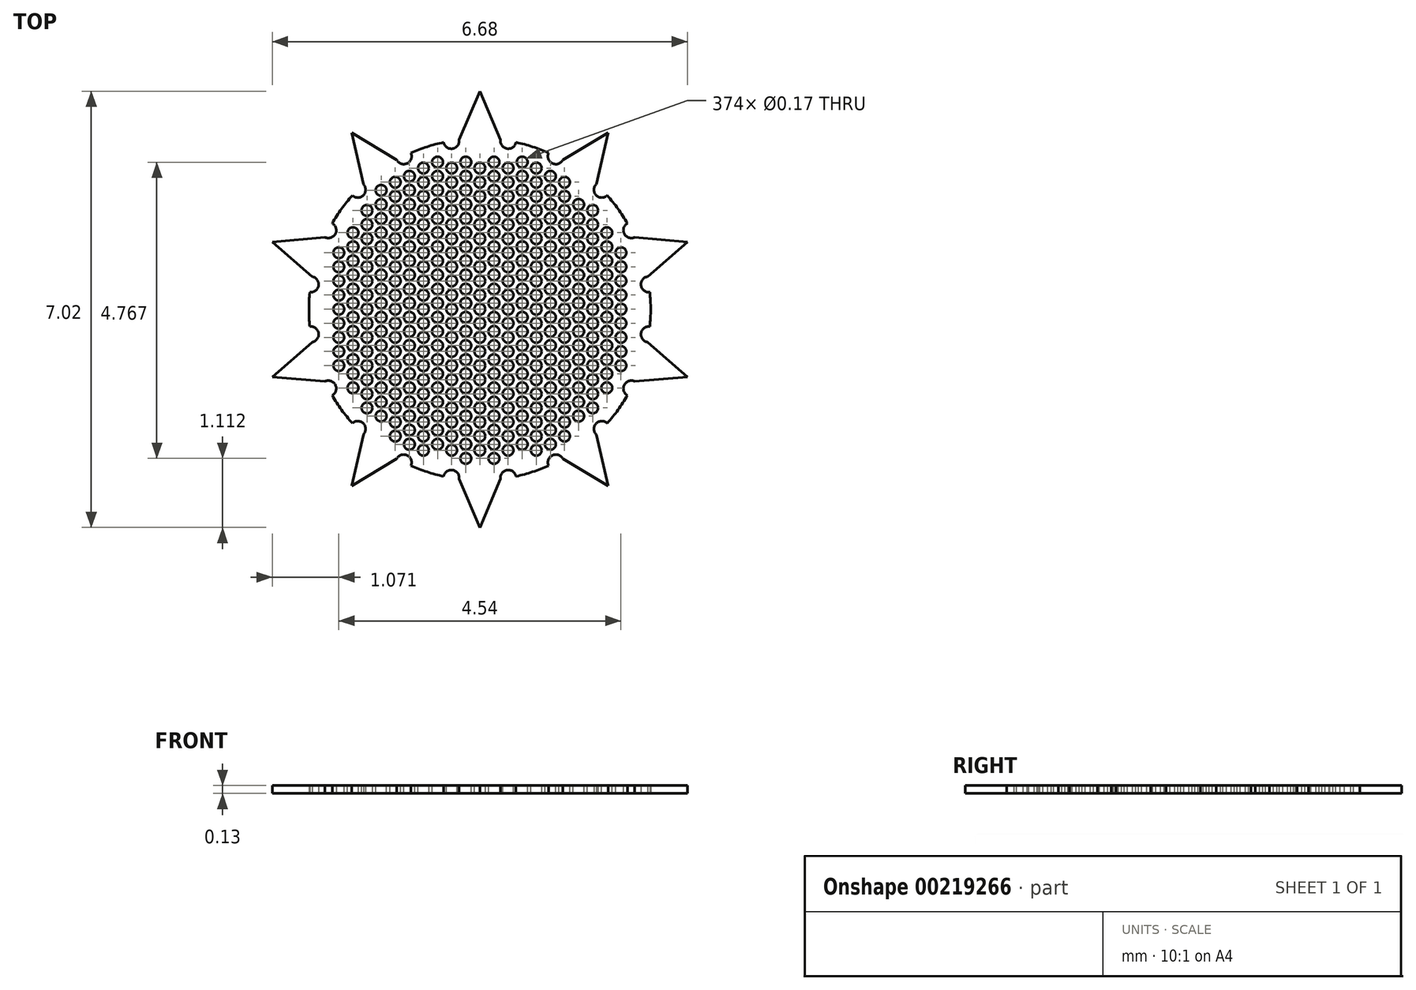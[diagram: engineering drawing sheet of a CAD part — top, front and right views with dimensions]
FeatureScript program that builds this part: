
annotation { "Feature Type Name" : "Feature", "Feature Type Description" : "" }
export const myFeature = defineFeature(function(context is Context, id is Id, definition is map)
    precondition{}
    {
        {
            var Q0;
            Q0=qCreatedBy(makeId("Top.planeOp"),FACE);
            var sketch = newSketch(context, id + "F0", { "sketchPlane" : qUnion([Q0])});
            skCircle(sketch, "E0", {"center": v(0, 0) * mm, "radius": 2.5 * mm});
            skArc(sketch, "E1", {"start": v(0.33, 2.73) * mm, "mid": v(0, 2.75) * mm, "end": v(-0.33, 2.73) * mm});
            skPoint(sketch, "E2", {"position": v(0, 2.75) * mm});
            skLineSegment(sketch, "E3", {"start": v(-3.94, 3.51) * mm, "end": v(3.7, 3.51) * mm, "construction": true});
            skLineSegment(sketch, "E4", {"start": v(0, 3.51) * mm, "end": v(-0.33, 2.73) * mm});
            skLineSegment(sketch, "E5", {"start": v(0, 3.51) * mm, "end": v(0.33, 2.73) * mm});
            skLineSegment(sketch, "E6.1.0", {"start": v(-2.06, 2.84) * mm, "end": v(-1.87, 2.01) * mm});
            skLineSegment(sketch, "E6.1.1", {"start": v(-2.06, 2.84) * mm, "end": v(-1.34, 2.4) * mm});
            skLineSegment(sketch, "E6.2.0", {"start": v(-3.34, 1.09) * mm, "end": v(-2.7, 0.53) * mm});
            skLineSegment(sketch, "E6.2.1", {"start": v(-3.34, 1.09) * mm, "end": v(-2.5, 1.16) * mm});
            skLineSegment(sketch, "E6.3.0", {"start": v(-3.34, -1.09) * mm, "end": v(-2.5, -1.16) * mm});
            skLineSegment(sketch, "E6.3.1", {"start": v(-3.34, -1.09) * mm, "end": v(-2.7, -0.53) * mm});
            skLineSegment(sketch, "E6.4.0", {"start": v(-2.06, -2.84) * mm, "end": v(-1.34, -2.4) * mm});
            skLineSegment(sketch, "E6.4.1", {"start": v(-2.06, -2.84) * mm, "end": v(-1.87, -2.01) * mm});
            skLineSegment(sketch, "E6.5.0", {"start": v(0, -3.51) * mm, "end": v(0.33, -2.73) * mm});
            skLineSegment(sketch, "E6.5.1", {"start": v(0, -3.51) * mm, "end": v(-0.33, -2.73) * mm});
            skLineSegment(sketch, "E6.6.0", {"start": v(2.06, -2.84) * mm, "end": v(1.87, -2.01) * mm});
            skLineSegment(sketch, "E6.6.1", {"start": v(2.06, -2.84) * mm, "end": v(1.34, -2.4) * mm});
            skLineSegment(sketch, "E6.7.0", {"start": v(3.34, -1.09) * mm, "end": v(2.7, -0.53) * mm});
            skLineSegment(sketch, "E6.7.1", {"start": v(3.34, -1.09) * mm, "end": v(2.5, -1.16) * mm});
            skLineSegment(sketch, "E6.8.0", {"start": v(3.34, 1.09) * mm, "end": v(2.5, 1.16) * mm});
            skLineSegment(sketch, "E6.8.1", {"start": v(3.34, 1.09) * mm, "end": v(2.7, 0.53) * mm});
            skLineSegment(sketch, "E6.9.0", {"start": v(2.06, 2.84) * mm, "end": v(1.34, 2.4) * mm});
            skLineSegment(sketch, "E6.9.1", {"start": v(2.06, 2.84) * mm, "end": v(1.87, 2.01) * mm});
            skCircle(sketch, "E7", {"center": v(0, 0) * mm, "radius": 2.62 * mm});
            skPoint(sketch, "E8", {"position": v(0.46, 2.71) * mm});
            skArc(sketch, "E9", {"start": v(0.33, 2.73) * mm, "mid": v(0.44, 2.59) * mm, "end": v(0.58, 2.69) * mm});
            skArc(sketch, "E10.1.0", {"start": v(-1.34, 2.4) * mm, "mid": v(-1.17, 2.35) * mm, "end": v(-1.1, 2.52) * mm});
            skArc(sketch, "E10.2.0", {"start": v(-2.5, 1.16) * mm, "mid": v(-2.32, 1.21) * mm, "end": v(-2.38, 1.38) * mm});
            skArc(sketch, "E10.3.0", {"start": v(-2.7, -0.53) * mm, "mid": v(-2.6, -0.38) * mm, "end": v(-2.74, -0.28) * mm});
            skArc(sketch, "E10.4.0", {"start": v(-1.87, -2.01) * mm, "mid": v(-1.87, -1.84) * mm, "end": v(-2.05, -1.83) * mm});
            skArc(sketch, "E10.5.0", {"start": v(-0.33, -2.73) * mm, "mid": v(-0.44, -2.59) * mm, "end": v(-0.58, -2.69) * mm});
            skArc(sketch, "E10.6.0", {"start": v(1.34, -2.4) * mm, "mid": v(1.17, -2.35) * mm, "end": v(1.1, -2.52) * mm});
            skArc(sketch, "E10.7.0", {"start": v(2.5, -1.16) * mm, "mid": v(2.32, -1.21) * mm, "end": v(2.38, -1.38) * mm});
            skArc(sketch, "E10.8.0", {"start": v(2.7, 0.53) * mm, "mid": v(2.6, 0.38) * mm, "end": v(2.74, 0.28) * mm});
            skArc(sketch, "E10.9.0", {"start": v(1.87, 2.01) * mm, "mid": v(1.87, 1.84) * mm, "end": v(2.05, 1.83) * mm});
            skArc(sketch, "E11", {"start": v(-0.58, 2.69) * mm, "mid": v(-0.44, 2.59) * mm, "end": v(-0.33, 2.73) * mm});
            skArc(sketch, "E12.trimOffspring", {"start": v(-0.58, 2.69) * mm, "mid": v(-0.85, 2.62) * mm, "end": v(-1.1, 2.52) * mm});
            skArc(sketch, "E13.1.0", {"start": v(-2.05, 1.83) * mm, "mid": v(-1.87, 1.84) * mm, "end": v(-1.87, 2.01) * mm});
            skArc(sketch, "E13.2.0", {"start": v(-2.74, 0.28) * mm, "mid": v(-2.6, 0.38) * mm, "end": v(-2.7, 0.53) * mm});
            skArc(sketch, "E13.3.0", {"start": v(-2.38, -1.38) * mm, "mid": v(-2.32, -1.21) * mm, "end": v(-2.5, -1.16) * mm});
            skArc(sketch, "E13.4.0", {"start": v(-1.1, -2.52) * mm, "mid": v(-1.17, -2.35) * mm, "end": v(-1.34, -2.4) * mm});
            skArc(sketch, "E13.5.0", {"start": v(0.58, -2.69) * mm, "mid": v(0.44, -2.59) * mm, "end": v(0.33, -2.73) * mm});
            skArc(sketch, "E13.6.0", {"start": v(2.05, -1.83) * mm, "mid": v(1.87, -1.84) * mm, "end": v(1.87, -2.01) * mm});
            skArc(sketch, "E13.7.0", {"start": v(2.74, -0.28) * mm, "mid": v(2.6, -0.38) * mm, "end": v(2.7, -0.53) * mm});
            skArc(sketch, "E13.8.0", {"start": v(2.38, 1.38) * mm, "mid": v(2.32, 1.21) * mm, "end": v(2.5, 1.16) * mm});
            skArc(sketch, "E13.9.0", {"start": v(1.1, 2.52) * mm, "mid": v(1.17, 2.35) * mm, "end": v(1.34, 2.4) * mm});
            skArc(sketch, "E14.trimOffspring", {"start": v(1.1, 2.52) * mm, "mid": v(0.85, 2.62) * mm, "end": v(0.58, 2.69) * mm});
            skArc(sketch, "E15.trimOffspring", {"start": v(1.87, 2.01) * mm, "mid": v(1.62, 2.22) * mm, "end": v(1.34, 2.4) * mm});
            skArc(sketch, "E16.trimOffspring", {"start": v(2.38, 1.38) * mm, "mid": v(2.22, 1.62) * mm, "end": v(2.05, 1.83) * mm});
            skArc(sketch, "E17.trimOffspring", {"start": v(2.7, 0.53) * mm, "mid": v(2.62, 0.85) * mm, "end": v(2.5, 1.16) * mm});
            skArc(sketch, "E18.trimOffspring", {"start": v(2.74, -0.28) * mm, "mid": v(2.75, 0) * mm, "end": v(2.74, 0.28) * mm});
            skArc(sketch, "E19.trimOffspring", {"start": v(2.5, -1.16) * mm, "mid": v(2.62, -0.85) * mm, "end": v(2.7, -0.53) * mm});
            skArc(sketch, "E20.trimOffspring", {"start": v(2.05, -1.83) * mm, "mid": v(2.22, -1.62) * mm, "end": v(2.38, -1.38) * mm});
            skArc(sketch, "E21.trimOffspring", {"start": v(1.34, -2.4) * mm, "mid": v(1.62, -2.22) * mm, "end": v(1.87, -2.01) * mm});
            skArc(sketch, "E22.trimOffspring", {"start": v(-2.38, -1.38) * mm, "mid": v(-2.22, -1.62) * mm, "end": v(-2.05, -1.83) * mm});
            skArc(sketch, "E23.trimOffspring", {"start": v(-1.87, -2.01) * mm, "mid": v(-1.62, -2.22) * mm, "end": v(-1.34, -2.4) * mm});
            skArc(sketch, "E24.trimOffspring", {"start": v(-1.1, -2.52) * mm, "mid": v(-0.85, -2.62) * mm, "end": v(-0.58, -2.69) * mm});
            skArc(sketch, "E25.trimOffspring", {"start": v(-0.33, -2.73) * mm, "mid": v(0, -2.75) * mm, "end": v(0.33, -2.73) * mm});
            skArc(sketch, "E26.trimOffspring", {"start": v(0.58, -2.69) * mm, "mid": v(0.85, -2.62) * mm, "end": v(1.1, -2.52) * mm});
            skArc(sketch, "E27.trimOffspring", {"start": v(-2.7, -0.53) * mm, "mid": v(-2.62, -0.85) * mm, "end": v(-2.5, -1.16) * mm});
            skArc(sketch, "E28.trimOffspring", {"start": v(-2.74, 0.28) * mm, "mid": v(-2.75, 0) * mm, "end": v(-2.74, -0.28) * mm});
            skArc(sketch, "E29.trimOffspring", {"start": v(-2.5, 1.16) * mm, "mid": v(-2.62, 0.85) * mm, "end": v(-2.7, 0.53) * mm});
            skArc(sketch, "E30.trimOffspring", {"start": v(-2.05, 1.83) * mm, "mid": v(-2.22, 1.62) * mm, "end": v(-2.38, 1.38) * mm});
            skArc(sketch, "E31.trimOffspring", {"start": v(-1.34, 2.4) * mm, "mid": v(-1.62, 2.22) * mm, "end": v(-1.87, 2.01) * mm});
            skSolve(sketch);
        }
        {
            var Q0;
            Q0=qSketchRegion(id+"F0",true);
            var Q1;
            Q1=makeQuery(id+"F0.imprint","IMPRINT",FACE,{"disambiguationData":[TD([[makeQuery(id+"F0.imprint","IMPRINT",EDGE,{"derivedFrom":sQuery(id+"F0.wireOp",EDGE,"E0")}),1.0]])]});
            extrude(context, id + "F1", {"entities" : qUnion([Q0, Q1]), "depth" : 0.13 * mm});
        }
        {
            var Q0;
            Q0=makeQuery(id+"F1.opExtrude","CAP_FACE",FACE,{"disambiguationData":[OSD([sQuery(id+"F0.wireOp",EDGE,"E1"),sQuery(id+"F0.wireOp",EDGE,"E4"),sQuery(id+"F0.wireOp",EDGE,"E5"),sQuery(id+"F0.wireOp",EDGE,"E6.1.0"),sQuery(id+"F0.wireOp",EDGE,"E6.1.1"),sQuery(id+"F0.wireOp",EDGE,"E6.2.0"),sQuery(id+"F0.wireOp",EDGE,"E6.2.1"),sQuery(id+"F0.wireOp",EDGE,"E6.3.0"),sQuery(id+"F0.wireOp",EDGE,"E6.3.1"),sQuery(id+"F0.wireOp",EDGE,"E6.4.0"),sQuery(id+"F0.wireOp",EDGE,"E6.4.1"),sQuery(id+"F0.wireOp",EDGE,"E6.5.0"),sQuery(id+"F0.wireOp",EDGE,"E6.5.1"),sQuery(id+"F0.wireOp",EDGE,"E6.6.0"),sQuery(id+"F0.wireOp",EDGE,"E6.6.1"),sQuery(id+"F0.wireOp",EDGE,"E6.7.0"),sQuery(id+"F0.wireOp",EDGE,"E6.7.1"),sQuery(id+"F0.wireOp",EDGE,"E6.8.0"),sQuery(id+"F0.wireOp",EDGE,"E6.8.1"),sQuery(id+"F0.wireOp",EDGE,"E6.9.0"),sQuery(id+"F0.wireOp",EDGE,"E6.9.1")])],"isStart":false});
            cPlane(context, id + "F2", {"entities" : qUnion([Q0]), "cplaneType" : CPlaneType.OFFSET, "offset" : 0 * mm, "width" : 150 * mm, "height" : 150 * mm});
        }
        {
            var Q0;
            Q0=qCreatedBy(id+"F2.planeOp",FACE);
            var sketch = newSketch(context, id + "F3", { "sketchPlane" : qUnion([Q0])});
            skCircle(sketch, "E32.2.1.8", {"center": v(-2.04, 1.23) * mm, "radius": 0.09 * mm});
            skCircle(sketch, "E32.2.1.9", {"center": v(-2.04, 1) * mm, "radius": 0.09 * mm});
            skCircle(sketch, "E32.0.1.10", {"center": v(-2.27, 0.91) * mm, "radius": 0.09 * mm});
            skCircle(sketch, "E32.2.1.10", {"center": v(-2.04, 0.78) * mm, "radius": 0.09 * mm});
            skCircle(sketch, "E32.2.2.5", {"center": v(-1.59, 1.91) * mm, "radius": 0.09 * mm});
            skCircle(sketch, "E32.2.2.6", {"center": v(-1.59, 1.69) * mm, "radius": 0.09 * mm});
            skCircle(sketch, "E32.0.2.7", {"center": v(-1.82, 1.6) * mm, "radius": 0.09 * mm});
            skCircle(sketch, "E32.2.2.7", {"center": v(-1.59, 1.46) * mm, "radius": 0.09 * mm});
            skCircle(sketch, "E32.0.2.8", {"center": v(-1.82, 1.36) * mm, "radius": 0.09 * mm});
            skCircle(sketch, "E32.2.2.8", {"center": v(-1.59, 1.23) * mm, "radius": 0.09 * mm});
            skCircle(sketch, "E32.0.2.9", {"center": v(-1.82, 1.14) * mm, "radius": 0.09 * mm});
            skCircle(sketch, "E32.2.2.9", {"center": v(-1.59, 1) * mm, "radius": 0.09 * mm});
            skCircle(sketch, "E32.0.2.10", {"center": v(-1.82, 0.91) * mm, "radius": 0.09 * mm});
            skCircle(sketch, "E32.2.2.10", {"center": v(-1.59, 0.78) * mm, "radius": 0.09 * mm});
            skCircle(sketch, "E32.2.3.4", {"center": v(-1.13, 2.14) * mm, "radius": 0.09 * mm});
            skCircle(sketch, "E32.0.3.5", {"center": v(-1.36, 2.05) * mm, "radius": 0.09 * mm});
            skCircle(sketch, "E32.2.3.5", {"center": v(-1.13, 1.91) * mm, "radius": 0.09 * mm});
            skCircle(sketch, "E32.0.3.6", {"center": v(-1.36, 1.82) * mm, "radius": 0.09 * mm});
            skCircle(sketch, "E32.2.3.6", {"center": v(-1.13, 1.69) * mm, "radius": 0.09 * mm});
            skCircle(sketch, "E32.0.3.7", {"center": v(-1.36, 1.6) * mm, "radius": 0.09 * mm});
            skCircle(sketch, "E32.2.3.7", {"center": v(-1.13, 1.46) * mm, "radius": 0.09 * mm});
            skCircle(sketch, "E32.0.3.8", {"center": v(-1.36, 1.36) * mm, "radius": 0.09 * mm});
            skCircle(sketch, "E32.2.3.8", {"center": v(-1.13, 1.23) * mm, "radius": 0.09 * mm});
            skCircle(sketch, "E32.0.3.9", {"center": v(-1.36, 1.14) * mm, "radius": 0.09 * mm});
            skCircle(sketch, "E32.2.3.9", {"center": v(-1.13, 1) * mm, "radius": 0.09 * mm});
            skCircle(sketch, "E32.0.3.10", {"center": v(-1.36, 0.91) * mm, "radius": 0.09 * mm});
            skCircle(sketch, "E32.2.3.10", {"center": v(-1.13, 0.78) * mm, "radius": 0.09 * mm});
            skCircle(sketch, "E32.2.4.3", {"center": v(-0.68, 2.37) * mm, "radius": 0.09 * mm});
            skCircle(sketch, "E32.0.4.4", {"center": v(-0.9, 2.27) * mm, "radius": 0.09 * mm});
            skCircle(sketch, "E32.2.4.4", {"center": v(-0.68, 2.14) * mm, "radius": 0.09 * mm});
            skCircle(sketch, "E32.0.4.5", {"center": v(-0.9, 2.05) * mm, "radius": 0.09 * mm});
            skCircle(sketch, "E32.2.4.5", {"center": v(-0.68, 1.91) * mm, "radius": 0.09 * mm});
            skCircle(sketch, "E32.0.4.6", {"center": v(-0.9, 1.82) * mm, "radius": 0.09 * mm});
            skCircle(sketch, "E32.2.4.6", {"center": v(-0.68, 1.69) * mm, "radius": 0.09 * mm});
            skCircle(sketch, "E32.0.4.7", {"center": v(-0.9, 1.6) * mm, "radius": 0.09 * mm});
            skCircle(sketch, "E32.2.4.7", {"center": v(-0.68, 1.46) * mm, "radius": 0.09 * mm});
            skCircle(sketch, "E32.0.4.8", {"center": v(-0.9, 1.36) * mm, "radius": 0.09 * mm});
            skCircle(sketch, "E32.2.4.8", {"center": v(-0.68, 1.23) * mm, "radius": 0.09 * mm});
            skCircle(sketch, "E32.0.4.9", {"center": v(-0.9, 1.14) * mm, "radius": 0.09 * mm});
            skCircle(sketch, "E32.2.4.9", {"center": v(-0.68, 1) * mm, "radius": 0.09 * mm});
            skCircle(sketch, "E32.0.4.10", {"center": v(-0.9, 0.91) * mm, "radius": 0.09 * mm});
            skCircle(sketch, "E32.2.4.10", {"center": v(-0.68, 0.78) * mm, "radius": 0.09 * mm});
            skCircle(sketch, "E32.2.5.3", {"center": v(-0.23, 2.37) * mm, "radius": 0.09 * mm});
            skCircle(sketch, "E32.0.5.4", {"center": v(-0.45, 2.27) * mm, "radius": 0.09 * mm});
            skCircle(sketch, "E32.2.5.4", {"center": v(-0.23, 2.14) * mm, "radius": 0.09 * mm});
            skCircle(sketch, "E32.0.5.5", {"center": v(-0.45, 2.05) * mm, "radius": 0.09 * mm});
            skCircle(sketch, "E32.2.5.5", {"center": v(-0.23, 1.91) * mm, "radius": 0.09 * mm});
            skCircle(sketch, "E32.0.5.6", {"center": v(-0.45, 1.82) * mm, "radius": 0.09 * mm});
            skCircle(sketch, "E32.2.5.6", {"center": v(-0.23, 1.69) * mm, "radius": 0.09 * mm});
            skCircle(sketch, "E32.0.5.7", {"center": v(-0.45, 1.6) * mm, "radius": 0.09 * mm});
            skCircle(sketch, "E32.2.5.7", {"center": v(-0.23, 1.46) * mm, "radius": 0.09 * mm});
            skCircle(sketch, "E32.0.5.8", {"center": v(-0.45, 1.36) * mm, "radius": 0.09 * mm});
            skCircle(sketch, "E32.2.5.8", {"center": v(-0.23, 1.23) * mm, "radius": 0.09 * mm});
            skCircle(sketch, "E32.0.5.9", {"center": v(-0.45, 1.14) * mm, "radius": 0.09 * mm});
            skCircle(sketch, "E32.2.5.9", {"center": v(-0.23, 1) * mm, "radius": 0.09 * mm});
            skCircle(sketch, "E32.0.5.10", {"center": v(-0.45, 0.91) * mm, "radius": 0.09 * mm});
            skCircle(sketch, "E32.2.5.10", {"center": v(-0.23, 0.78) * mm, "radius": 0.09 * mm});
            skCircle(sketch, "E32.2.6.3", {"center": v(0.23, 2.37) * mm, "radius": 0.09 * mm});
            skCircle(sketch, "E32.0.6.4", {"center": v(0, 2.27) * mm, "radius": 0.09 * mm});
            skCircle(sketch, "E32.2.6.4", {"center": v(0.23, 2.14) * mm, "radius": 0.09 * mm});
            skCircle(sketch, "E32.0.6.5", {"center": v(0, 2.05) * mm, "radius": 0.09 * mm});
            skCircle(sketch, "E32.2.6.5", {"center": v(0.23, 1.91) * mm, "radius": 0.09 * mm});
            skCircle(sketch, "E32.0.6.6", {"center": v(0, 1.82) * mm, "radius": 0.09 * mm});
            skCircle(sketch, "E32.2.6.6", {"center": v(0.23, 1.69) * mm, "radius": 0.09 * mm});
            skCircle(sketch, "E32.0.6.7", {"center": v(0, 1.6) * mm, "radius": 0.09 * mm});
            skCircle(sketch, "E32.2.6.7", {"center": v(0.23, 1.46) * mm, "radius": 0.09 * mm});
            skCircle(sketch, "E32.0.6.8", {"center": v(0, 1.36) * mm, "radius": 0.09 * mm});
            skCircle(sketch, "E32.2.6.8", {"center": v(0.23, 1.23) * mm, "radius": 0.09 * mm});
            skCircle(sketch, "E32.0.6.9", {"center": v(0, 1.14) * mm, "radius": 0.09 * mm});
            skCircle(sketch, "E32.2.6.9", {"center": v(0.23, 1) * mm, "radius": 0.09 * mm});
            skCircle(sketch, "E32.0.6.10", {"center": v(0, 0.91) * mm, "radius": 0.09 * mm});
            skCircle(sketch, "E32.2.6.10", {"center": v(0.23, 0.78) * mm, "radius": 0.09 * mm});
            skCircle(sketch, "E32.2.7.3", {"center": v(0.68, 2.37) * mm, "radius": 0.09 * mm});
            skCircle(sketch, "E32.0.7.4", {"center": v(0.45, 2.27) * mm, "radius": 0.09 * mm});
            skCircle(sketch, "E32.2.7.4", {"center": v(0.68, 2.14) * mm, "radius": 0.09 * mm});
            skCircle(sketch, "E32.0.7.5", {"center": v(0.45, 2.05) * mm, "radius": 0.09 * mm});
            skCircle(sketch, "E32.2.7.5", {"center": v(0.68, 1.91) * mm, "radius": 0.09 * mm});
            skCircle(sketch, "E32.0.7.6", {"center": v(0.45, 1.82) * mm, "radius": 0.09 * mm});
            skCircle(sketch, "E32.2.7.6", {"center": v(0.68, 1.69) * mm, "radius": 0.09 * mm});
            skCircle(sketch, "E32.0.7.7", {"center": v(0.45, 1.6) * mm, "radius": 0.09 * mm});
            skCircle(sketch, "E32.2.7.7", {"center": v(0.68, 1.46) * mm, "radius": 0.09 * mm});
            skCircle(sketch, "E32.0.7.8", {"center": v(0.45, 1.36) * mm, "radius": 0.09 * mm});
            skCircle(sketch, "E32.2.7.8", {"center": v(0.68, 1.23) * mm, "radius": 0.09 * mm});
            skCircle(sketch, "E32.0.7.9", {"center": v(0.45, 1.14) * mm, "radius": 0.09 * mm});
            skCircle(sketch, "E32.2.7.9", {"center": v(0.68, 1) * mm, "radius": 0.09 * mm});
            skCircle(sketch, "E32.0.7.10", {"center": v(0.45, 0.91) * mm, "radius": 0.09 * mm});
            skCircle(sketch, "E32.2.7.10", {"center": v(0.68, 0.78) * mm, "radius": 0.09 * mm});
            skCircle(sketch, "E32.0.8.4", {"center": v(0.9, 2.27) * mm, "radius": 0.09 * mm});
            skCircle(sketch, "E32.2.8.4", {"center": v(1.14, 2.14) * mm, "radius": 0.09 * mm});
            skCircle(sketch, "E32.0.8.5", {"center": v(0.9, 2.05) * mm, "radius": 0.09 * mm});
            skCircle(sketch, "E32.2.8.5", {"center": v(1.14, 1.91) * mm, "radius": 0.09 * mm});
            skCircle(sketch, "E32.0.8.6", {"center": v(0.9, 1.82) * mm, "radius": 0.09 * mm});
            skCircle(sketch, "E32.2.8.6", {"center": v(1.14, 1.69) * mm, "radius": 0.09 * mm});
            skCircle(sketch, "E32.0.8.7", {"center": v(0.9, 1.6) * mm, "radius": 0.09 * mm});
            skCircle(sketch, "E32.2.8.7", {"center": v(1.14, 1.46) * mm, "radius": 0.09 * mm});
            skCircle(sketch, "E32.0.8.8", {"center": v(0.9, 1.36) * mm, "radius": 0.09 * mm});
            skCircle(sketch, "E32.2.8.8", {"center": v(1.14, 1.23) * mm, "radius": 0.09 * mm});
            skCircle(sketch, "E32.0.8.9", {"center": v(0.9, 1.14) * mm, "radius": 0.09 * mm});
            skCircle(sketch, "E32.2.8.9", {"center": v(1.14, 1) * mm, "radius": 0.09 * mm});
            skCircle(sketch, "E32.0.8.10", {"center": v(0.9, 0.91) * mm, "radius": 0.09 * mm});
            skCircle(sketch, "E32.2.8.10", {"center": v(1.14, 0.78) * mm, "radius": 0.09 * mm});
            skCircle(sketch, "E32.0.9.5", {"center": v(1.36, 2.05) * mm, "radius": 0.09 * mm});
            skCircle(sketch, "E32.0.9.6", {"center": v(1.36, 1.82) * mm, "radius": 0.09 * mm});
            skCircle(sketch, "E32.2.9.6", {"center": v(1.6, 1.69) * mm, "radius": 0.09 * mm});
            skCircle(sketch, "E32.0.9.7", {"center": v(1.36, 1.6) * mm, "radius": 0.09 * mm});
            skCircle(sketch, "E32.2.9.7", {"center": v(1.6, 1.46) * mm, "radius": 0.09 * mm});
            skCircle(sketch, "E32.0.9.8", {"center": v(1.36, 1.36) * mm, "radius": 0.09 * mm});
            skCircle(sketch, "E32.2.9.8", {"center": v(1.6, 1.23) * mm, "radius": 0.09 * mm});
            skCircle(sketch, "E32.0.9.9", {"center": v(1.36, 1.14) * mm, "radius": 0.09 * mm});
            skCircle(sketch, "E32.2.9.9", {"center": v(1.6, 1) * mm, "radius": 0.09 * mm});
            skCircle(sketch, "E32.0.9.10", {"center": v(1.36, 0.91) * mm, "radius": 0.09 * mm});
            skCircle(sketch, "E32.2.9.10", {"center": v(1.6, 0.78) * mm, "radius": 0.09 * mm});
            skCircle(sketch, "E32.0.10.7", {"center": v(1.82, 1.6) * mm, "radius": 0.09 * mm});
            skCircle(sketch, "E32.0.10.8", {"center": v(1.82, 1.36) * mm, "radius": 0.09 * mm});
            skCircle(sketch, "E32.2.10.8", {"center": v(2.04, 1.23) * mm, "radius": 0.09 * mm});
            skCircle(sketch, "E32.0.10.9", {"center": v(1.82, 1.14) * mm, "radius": 0.09 * mm});
            skCircle(sketch, "E32.2.10.9", {"center": v(2.04, 1) * mm, "radius": 0.09 * mm});
            skCircle(sketch, "E32.0.10.10", {"center": v(1.82, 0.91) * mm, "radius": 0.09 * mm});
            skCircle(sketch, "E32.2.10.10", {"center": v(2.04, 0.78) * mm, "radius": 0.09 * mm});
            skCircle(sketch, "E33.0.1.11", {"center": v(-2.27, 0.68) * mm, "radius": 0.09 * mm});
            skCircle(sketch, "E33.2.1.11", {"center": v(-2.04, 0.55) * mm, "radius": 0.09 * mm});
            skCircle(sketch, "E33.0.1.12", {"center": v(-2.27, 0.46) * mm, "radius": 0.09 * mm});
            skCircle(sketch, "E33.2.1.12", {"center": v(-2.04, 0.33) * mm, "radius": 0.09 * mm});
            skCircle(sketch, "E33.0.1.13", {"center": v(-2.27, 0.23) * mm, "radius": 0.09 * mm});
            skCircle(sketch, "E33.2.1.13", {"center": v(-2.04, 0.1) * mm, "radius": 0.09 * mm});
            skCircle(sketch, "E33.0.1.14", {"center": v(-2.27, 0) * mm, "radius": 0.09 * mm});
            skCircle(sketch, "E33.2.1.14", {"center": v(-2.04, -0.13) * mm, "radius": 0.09 * mm});
            skCircle(sketch, "E33.0.1.15", {"center": v(-2.27, -0.22) * mm, "radius": 0.09 * mm});
            skCircle(sketch, "E33.2.1.15", {"center": v(-2.04, -0.36) * mm, "radius": 0.09 * mm});
            skCircle(sketch, "E33.0.1.16", {"center": v(-2.27, -0.45) * mm, "radius": 0.09 * mm});
            skCircle(sketch, "E33.2.1.16", {"center": v(-2.04, -0.58) * mm, "radius": 0.09 * mm});
            skCircle(sketch, "E33.0.1.17", {"center": v(-2.27, -0.68) * mm, "radius": 0.09 * mm});
            skCircle(sketch, "E33.2.1.17", {"center": v(-2.04, -0.8) * mm, "radius": 0.09 * mm});
            skCircle(sketch, "E33.0.1.18", {"center": v(-2.27, -0.9) * mm, "radius": 0.09 * mm});
            skCircle(sketch, "E33.2.1.18", {"center": v(-2.04, -1.04) * mm, "radius": 0.09 * mm});
            skCircle(sketch, "E33.2.1.19", {"center": v(-2.04, -1.26) * mm, "radius": 0.09 * mm});
            skCircle(sketch, "E33.0.2.11", {"center": v(-1.82, 0.68) * mm, "radius": 0.09 * mm});
            skCircle(sketch, "E33.2.2.11", {"center": v(-1.59, 0.55) * mm, "radius": 0.09 * mm});
            skCircle(sketch, "E33.0.2.12", {"center": v(-1.82, 0.46) * mm, "radius": 0.09 * mm});
            skCircle(sketch, "E33.2.2.12", {"center": v(-1.59, 0.33) * mm, "radius": 0.09 * mm});
            skCircle(sketch, "E33.0.2.13", {"center": v(-1.82, 0.23) * mm, "radius": 0.09 * mm});
            skCircle(sketch, "E33.2.2.13", {"center": v(-1.59, 0.1) * mm, "radius": 0.09 * mm});
            skCircle(sketch, "E33.0.2.14", {"center": v(-1.82, 0) * mm, "radius": 0.09 * mm});
            skCircle(sketch, "E33.2.2.14", {"center": v(-1.59, -0.13) * mm, "radius": 0.09 * mm});
            skCircle(sketch, "E33.0.2.15", {"center": v(-1.82, -0.22) * mm, "radius": 0.09 * mm});
            skCircle(sketch, "E33.2.2.15", {"center": v(-1.59, -0.36) * mm, "radius": 0.09 * mm});
            skCircle(sketch, "E33.0.2.16", {"center": v(-1.82, -0.45) * mm, "radius": 0.09 * mm});
            skCircle(sketch, "E33.2.2.16", {"center": v(-1.59, -0.58) * mm, "radius": 0.09 * mm});
            skCircle(sketch, "E33.0.2.17", {"center": v(-1.82, -0.68) * mm, "radius": 0.09 * mm});
            skCircle(sketch, "E33.2.2.17", {"center": v(-1.59, -0.8) * mm, "radius": 0.09 * mm});
            skCircle(sketch, "E33.0.2.18", {"center": v(-1.82, -0.9) * mm, "radius": 0.09 * mm});
            skCircle(sketch, "E33.2.2.18", {"center": v(-1.59, -1.04) * mm, "radius": 0.09 * mm});
            skCircle(sketch, "E33.0.2.19", {"center": v(-1.82, -1.13) * mm, "radius": 0.09 * mm});
            skCircle(sketch, "E33.2.2.19", {"center": v(-1.59, -1.26) * mm, "radius": 0.09 * mm});
            skCircle(sketch, "E33.0.2.20", {"center": v(-1.82, -1.36) * mm, "radius": 0.09 * mm});
            skCircle(sketch, "E33.2.2.20", {"center": v(-1.59, -1.5) * mm, "radius": 0.09 * mm});
            skCircle(sketch, "E33.0.2.21", {"center": v(-1.82, -1.59) * mm, "radius": 0.09 * mm});
            skCircle(sketch, "E33.2.2.21", {"center": v(-1.59, -1.72) * mm, "radius": 0.09 * mm});
            skCircle(sketch, "E33.0.3.11", {"center": v(-1.36, 0.68) * mm, "radius": 0.09 * mm});
            skCircle(sketch, "E33.2.3.11", {"center": v(-1.13, 0.55) * mm, "radius": 0.09 * mm});
            skCircle(sketch, "E33.0.3.12", {"center": v(-1.36, 0.46) * mm, "radius": 0.09 * mm});
            skCircle(sketch, "E33.2.3.12", {"center": v(-1.13, 0.33) * mm, "radius": 0.09 * mm});
            skCircle(sketch, "E33.0.3.13", {"center": v(-1.36, 0.23) * mm, "radius": 0.09 * mm});
            skCircle(sketch, "E33.2.3.13", {"center": v(-1.13, 0.1) * mm, "radius": 0.09 * mm});
            skCircle(sketch, "E33.0.3.14", {"center": v(-1.36, 0) * mm, "radius": 0.09 * mm});
            skCircle(sketch, "E33.2.3.14", {"center": v(-1.13, -0.13) * mm, "radius": 0.09 * mm});
            skCircle(sketch, "E33.0.3.15", {"center": v(-1.36, -0.22) * mm, "radius": 0.09 * mm});
            skCircle(sketch, "E33.2.3.15", {"center": v(-1.13, -0.36) * mm, "radius": 0.09 * mm});
            skCircle(sketch, "E33.0.3.16", {"center": v(-1.36, -0.45) * mm, "radius": 0.09 * mm});
            skCircle(sketch, "E33.2.3.16", {"center": v(-1.13, -0.58) * mm, "radius": 0.09 * mm});
            skCircle(sketch, "E33.0.3.17", {"center": v(-1.36, -0.68) * mm, "radius": 0.09 * mm});
            skCircle(sketch, "E33.2.3.17", {"center": v(-1.13, -0.8) * mm, "radius": 0.09 * mm});
            skCircle(sketch, "E33.0.3.18", {"center": v(-1.36, -0.9) * mm, "radius": 0.09 * mm});
            skCircle(sketch, "E33.2.3.18", {"center": v(-1.13, -1.04) * mm, "radius": 0.09 * mm});
            skCircle(sketch, "E33.0.3.19", {"center": v(-1.36, -1.13) * mm, "radius": 0.09 * mm});
            skCircle(sketch, "E33.2.3.19", {"center": v(-1.13, -1.26) * mm, "radius": 0.09 * mm});
            skCircle(sketch, "E33.0.3.20", {"center": v(-1.36, -1.36) * mm, "radius": 0.09 * mm});
            skCircle(sketch, "E33.2.3.20", {"center": v(-1.13, -1.5) * mm, "radius": 0.09 * mm});
            skCircle(sketch, "E33.0.3.21", {"center": v(-1.36, -1.59) * mm, "radius": 0.09 * mm});
            skCircle(sketch, "E33.2.3.21", {"center": v(-1.13, -1.72) * mm, "radius": 0.09 * mm});
            skCircle(sketch, "E33.0.4.11", {"center": v(-0.9, 0.68) * mm, "radius": 0.09 * mm});
            skCircle(sketch, "E33.2.4.11", {"center": v(-0.68, 0.55) * mm, "radius": 0.09 * mm});
            skCircle(sketch, "E33.0.4.12", {"center": v(-0.9, 0.46) * mm, "radius": 0.09 * mm});
            skCircle(sketch, "E33.2.4.12", {"center": v(-0.68, 0.33) * mm, "radius": 0.09 * mm});
            skCircle(sketch, "E33.0.4.13", {"center": v(-0.9, 0.23) * mm, "radius": 0.09 * mm});
            skCircle(sketch, "E33.2.4.13", {"center": v(-0.68, 0.1) * mm, "radius": 0.09 * mm});
            skCircle(sketch, "E33.0.4.14", {"center": v(-0.9, 0) * mm, "radius": 0.09 * mm});
            skCircle(sketch, "E33.2.4.14", {"center": v(-0.68, -0.13) * mm, "radius": 0.09 * mm});
            skCircle(sketch, "E33.0.4.15", {"center": v(-0.9, -0.22) * mm, "radius": 0.09 * mm});
            skCircle(sketch, "E33.2.4.15", {"center": v(-0.68, -0.36) * mm, "radius": 0.09 * mm});
            skCircle(sketch, "E33.0.4.16", {"center": v(-0.9, -0.45) * mm, "radius": 0.09 * mm});
            skCircle(sketch, "E33.2.4.16", {"center": v(-0.68, -0.58) * mm, "radius": 0.09 * mm});
            skCircle(sketch, "E33.0.4.17", {"center": v(-0.9, -0.68) * mm, "radius": 0.09 * mm});
            skCircle(sketch, "E33.2.4.17", {"center": v(-0.68, -0.8) * mm, "radius": 0.09 * mm});
            skCircle(sketch, "E33.0.4.18", {"center": v(-0.9, -0.9) * mm, "radius": 0.09 * mm});
            skCircle(sketch, "E33.2.4.18", {"center": v(-0.68, -1.04) * mm, "radius": 0.09 * mm});
            skCircle(sketch, "E33.0.4.19", {"center": v(-0.9, -1.13) * mm, "radius": 0.09 * mm});
            skCircle(sketch, "E33.2.4.19", {"center": v(-0.68, -1.26) * mm, "radius": 0.09 * mm});
            skCircle(sketch, "E33.0.4.20", {"center": v(-0.9, -1.36) * mm, "radius": 0.09 * mm});
            skCircle(sketch, "E33.2.4.20", {"center": v(-0.68, -1.5) * mm, "radius": 0.09 * mm});
            skCircle(sketch, "E33.0.4.21", {"center": v(-0.9, -1.59) * mm, "radius": 0.09 * mm});
            skCircle(sketch, "E33.2.4.21", {"center": v(-0.68, -1.72) * mm, "radius": 0.09 * mm});
            skCircle(sketch, "E33.0.5.11", {"center": v(-0.45, 0.68) * mm, "radius": 0.09 * mm});
            skCircle(sketch, "E33.2.5.11", {"center": v(-0.23, 0.55) * mm, "radius": 0.09 * mm});
            skCircle(sketch, "E33.0.5.12", {"center": v(-0.45, 0.46) * mm, "radius": 0.09 * mm});
            skCircle(sketch, "E33.2.5.12", {"center": v(-0.23, 0.33) * mm, "radius": 0.09 * mm});
            skCircle(sketch, "E33.0.5.13", {"center": v(-0.45, 0.23) * mm, "radius": 0.09 * mm});
            skCircle(sketch, "E33.2.5.13", {"center": v(-0.23, 0.1) * mm, "radius": 0.09 * mm});
            skCircle(sketch, "E33.0.5.14", {"center": v(-0.45, 0) * mm, "radius": 0.09 * mm});
            skCircle(sketch, "E33.2.5.14", {"center": v(-0.23, -0.13) * mm, "radius": 0.09 * mm});
            skCircle(sketch, "E33.0.5.15", {"center": v(-0.45, -0.22) * mm, "radius": 0.09 * mm});
            skCircle(sketch, "E33.2.5.15", {"center": v(-0.23, -0.36) * mm, "radius": 0.09 * mm});
            skCircle(sketch, "E33.0.5.16", {"center": v(-0.45, -0.45) * mm, "radius": 0.09 * mm});
            skCircle(sketch, "E33.2.5.16", {"center": v(-0.23, -0.58) * mm, "radius": 0.09 * mm});
            skCircle(sketch, "E33.0.5.17", {"center": v(-0.45, -0.68) * mm, "radius": 0.09 * mm});
            skCircle(sketch, "E33.2.5.17", {"center": v(-0.23, -0.8) * mm, "radius": 0.09 * mm});
            skCircle(sketch, "E33.0.5.18", {"center": v(-0.45, -0.9) * mm, "radius": 0.09 * mm});
            skCircle(sketch, "E33.2.5.18", {"center": v(-0.23, -1.04) * mm, "radius": 0.09 * mm});
            skCircle(sketch, "E33.0.5.19", {"center": v(-0.45, -1.13) * mm, "radius": 0.09 * mm});
            skCircle(sketch, "E33.2.5.19", {"center": v(-0.23, -1.26) * mm, "radius": 0.09 * mm});
            skCircle(sketch, "E33.0.5.20", {"center": v(-0.45, -1.36) * mm, "radius": 0.09 * mm});
            skCircle(sketch, "E33.2.5.20", {"center": v(-0.23, -1.5) * mm, "radius": 0.09 * mm});
            skCircle(sketch, "E33.0.5.21", {"center": v(-0.45, -1.59) * mm, "radius": 0.09 * mm});
            skCircle(sketch, "E33.2.5.21", {"center": v(-0.23, -1.72) * mm, "radius": 0.09 * mm});
            skCircle(sketch, "E33.0.6.11", {"center": v(0, 0.68) * mm, "radius": 0.09 * mm});
            skCircle(sketch, "E33.2.6.11", {"center": v(0.23, 0.55) * mm, "radius": 0.09 * mm});
            skCircle(sketch, "E33.0.6.12", {"center": v(0, 0.46) * mm, "radius": 0.09 * mm});
            skCircle(sketch, "E33.2.6.12", {"center": v(0.23, 0.33) * mm, "radius": 0.09 * mm});
            skCircle(sketch, "E33.0.6.13", {"center": v(0, 0.23) * mm, "radius": 0.09 * mm});
            skCircle(sketch, "E33.2.6.13", {"center": v(0.23, 0.1) * mm, "radius": 0.09 * mm});
            skCircle(sketch, "E33.0.6.14", {"center": v(0, 0) * mm, "radius": 0.09 * mm});
            skCircle(sketch, "E33.2.6.14", {"center": v(0.23, -0.13) * mm, "radius": 0.09 * mm});
            skCircle(sketch, "E33.0.6.15", {"center": v(0, -0.22) * mm, "radius": 0.09 * mm});
            skCircle(sketch, "E33.2.6.15", {"center": v(0.23, -0.36) * mm, "radius": 0.09 * mm});
            skCircle(sketch, "E33.0.6.16", {"center": v(0, -0.45) * mm, "radius": 0.09 * mm});
            skCircle(sketch, "E33.2.6.16", {"center": v(0.23, -0.58) * mm, "radius": 0.09 * mm});
            skCircle(sketch, "E33.0.6.17", {"center": v(0, -0.68) * mm, "radius": 0.09 * mm});
            skCircle(sketch, "E33.2.6.17", {"center": v(0.23, -0.8) * mm, "radius": 0.09 * mm});
            skCircle(sketch, "E33.0.6.18", {"center": v(0, -0.9) * mm, "radius": 0.09 * mm});
            skCircle(sketch, "E33.2.6.18", {"center": v(0.23, -1.04) * mm, "radius": 0.09 * mm});
            skCircle(sketch, "E33.0.6.19", {"center": v(0, -1.13) * mm, "radius": 0.09 * mm});
            skCircle(sketch, "E33.2.6.19", {"center": v(0.23, -1.26) * mm, "radius": 0.09 * mm});
            skCircle(sketch, "E33.0.6.20", {"center": v(0, -1.36) * mm, "radius": 0.09 * mm});
            skCircle(sketch, "E33.2.6.20", {"center": v(0.23, -1.5) * mm, "radius": 0.09 * mm});
            skCircle(sketch, "E33.0.6.21", {"center": v(0, -1.59) * mm, "radius": 0.09 * mm});
            skCircle(sketch, "E33.2.6.21", {"center": v(0.23, -1.72) * mm, "radius": 0.09 * mm});
            skCircle(sketch, "E33.0.7.11", {"center": v(0.45, 0.68) * mm, "radius": 0.09 * mm});
            skCircle(sketch, "E33.2.7.11", {"center": v(0.68, 0.55) * mm, "radius": 0.09 * mm});
            skCircle(sketch, "E33.0.7.12", {"center": v(0.45, 0.46) * mm, "radius": 0.09 * mm});
            skCircle(sketch, "E33.2.7.12", {"center": v(0.68, 0.33) * mm, "radius": 0.09 * mm});
            skCircle(sketch, "E33.0.7.13", {"center": v(0.45, 0.23) * mm, "radius": 0.09 * mm});
            skCircle(sketch, "E33.2.7.13", {"center": v(0.68, 0.1) * mm, "radius": 0.09 * mm});
            skCircle(sketch, "E33.0.7.14", {"center": v(0.45, 0) * mm, "radius": 0.09 * mm});
            skCircle(sketch, "E33.2.7.14", {"center": v(0.68, -0.13) * mm, "radius": 0.09 * mm});
            skCircle(sketch, "E33.0.7.15", {"center": v(0.45, -0.22) * mm, "radius": 0.09 * mm});
            skCircle(sketch, "E33.2.7.15", {"center": v(0.68, -0.36) * mm, "radius": 0.09 * mm});
            skCircle(sketch, "E33.0.7.16", {"center": v(0.45, -0.45) * mm, "radius": 0.09 * mm});
            skCircle(sketch, "E33.2.7.16", {"center": v(0.68, -0.58) * mm, "radius": 0.09 * mm});
            skCircle(sketch, "E33.0.7.17", {"center": v(0.45, -0.68) * mm, "radius": 0.09 * mm});
            skCircle(sketch, "E33.2.7.17", {"center": v(0.68, -0.8) * mm, "radius": 0.09 * mm});
            skCircle(sketch, "E33.0.7.18", {"center": v(0.45, -0.9) * mm, "radius": 0.09 * mm});
            skCircle(sketch, "E33.2.7.18", {"center": v(0.68, -1.04) * mm, "radius": 0.09 * mm});
            skCircle(sketch, "E33.0.7.19", {"center": v(0.45, -1.13) * mm, "radius": 0.09 * mm});
            skCircle(sketch, "E33.2.7.19", {"center": v(0.68, -1.26) * mm, "radius": 0.09 * mm});
            skCircle(sketch, "E33.0.7.20", {"center": v(0.45, -1.36) * mm, "radius": 0.09 * mm});
            skCircle(sketch, "E33.2.7.20", {"center": v(0.68, -1.5) * mm, "radius": 0.09 * mm});
            skCircle(sketch, "E33.0.7.21", {"center": v(0.45, -1.59) * mm, "radius": 0.09 * mm});
            skCircle(sketch, "E33.2.7.21", {"center": v(0.68, -1.72) * mm, "radius": 0.09 * mm});
            skCircle(sketch, "E33.0.8.11", {"center": v(0.9, 0.68) * mm, "radius": 0.09 * mm});
            skCircle(sketch, "E33.2.8.11", {"center": v(1.14, 0.55) * mm, "radius": 0.09 * mm});
            skCircle(sketch, "E33.0.8.12", {"center": v(0.9, 0.46) * mm, "radius": 0.09 * mm});
            skCircle(sketch, "E33.2.8.12", {"center": v(1.14, 0.33) * mm, "radius": 0.09 * mm});
            skCircle(sketch, "E33.0.8.13", {"center": v(0.9, 0.23) * mm, "radius": 0.09 * mm});
            skCircle(sketch, "E33.2.8.13", {"center": v(1.14, 0.1) * mm, "radius": 0.09 * mm});
            skCircle(sketch, "E33.0.8.14", {"center": v(0.9, 0) * mm, "radius": 0.09 * mm});
            skCircle(sketch, "E33.2.8.14", {"center": v(1.14, -0.13) * mm, "radius": 0.09 * mm});
            skCircle(sketch, "E33.0.8.15", {"center": v(0.9, -0.22) * mm, "radius": 0.09 * mm});
            skCircle(sketch, "E33.2.8.15", {"center": v(1.14, -0.36) * mm, "radius": 0.09 * mm});
            skCircle(sketch, "E33.0.8.16", {"center": v(0.9, -0.45) * mm, "radius": 0.09 * mm});
            skCircle(sketch, "E33.2.8.16", {"center": v(1.14, -0.58) * mm, "radius": 0.09 * mm});
            skCircle(sketch, "E33.0.8.17", {"center": v(0.9, -0.68) * mm, "radius": 0.09 * mm});
            skCircle(sketch, "E33.2.8.17", {"center": v(1.14, -0.8) * mm, "radius": 0.09 * mm});
            skCircle(sketch, "E33.0.8.18", {"center": v(0.9, -0.9) * mm, "radius": 0.09 * mm});
            skCircle(sketch, "E33.2.8.18", {"center": v(1.14, -1.04) * mm, "radius": 0.09 * mm});
            skCircle(sketch, "E33.0.8.19", {"center": v(0.9, -1.13) * mm, "radius": 0.09 * mm});
            skCircle(sketch, "E33.2.8.19", {"center": v(1.14, -1.26) * mm, "radius": 0.09 * mm});
            skCircle(sketch, "E33.0.8.20", {"center": v(0.9, -1.36) * mm, "radius": 0.09 * mm});
            skCircle(sketch, "E33.2.8.20", {"center": v(1.14, -1.5) * mm, "radius": 0.09 * mm});
            skCircle(sketch, "E33.0.8.21", {"center": v(0.9, -1.59) * mm, "radius": 0.09 * mm});
            skCircle(sketch, "E33.2.8.21", {"center": v(1.14, -1.72) * mm, "radius": 0.09 * mm});
            skCircle(sketch, "E33.0.9.11", {"center": v(1.36, 0.68) * mm, "radius": 0.09 * mm});
            skCircle(sketch, "E33.2.9.11", {"center": v(1.6, 0.55) * mm, "radius": 0.09 * mm});
            skCircle(sketch, "E33.0.9.12", {"center": v(1.36, 0.46) * mm, "radius": 0.09 * mm});
            skCircle(sketch, "E33.2.9.12", {"center": v(1.6, 0.33) * mm, "radius": 0.09 * mm});
            skCircle(sketch, "E33.0.9.13", {"center": v(1.36, 0.23) * mm, "radius": 0.09 * mm});
            skCircle(sketch, "E33.2.9.13", {"center": v(1.6, 0.1) * mm, "radius": 0.09 * mm});
            skCircle(sketch, "E33.0.9.14", {"center": v(1.36, 0) * mm, "radius": 0.09 * mm});
            skCircle(sketch, "E33.2.9.14", {"center": v(1.6, -0.13) * mm, "radius": 0.09 * mm});
            skCircle(sketch, "E33.0.9.15", {"center": v(1.36, -0.22) * mm, "radius": 0.09 * mm});
            skCircle(sketch, "E33.2.9.15", {"center": v(1.6, -0.36) * mm, "radius": 0.09 * mm});
            skCircle(sketch, "E33.0.9.16", {"center": v(1.36, -0.45) * mm, "radius": 0.09 * mm});
            skCircle(sketch, "E33.2.9.16", {"center": v(1.6, -0.58) * mm, "radius": 0.09 * mm});
            skCircle(sketch, "E33.0.9.17", {"center": v(1.36, -0.68) * mm, "radius": 0.09 * mm});
            skCircle(sketch, "E33.2.9.17", {"center": v(1.6, -0.8) * mm, "radius": 0.09 * mm});
            skCircle(sketch, "E33.0.9.18", {"center": v(1.36, -0.9) * mm, "radius": 0.09 * mm});
            skCircle(sketch, "E33.2.9.18", {"center": v(1.6, -1.04) * mm, "radius": 0.09 * mm});
            skCircle(sketch, "E33.0.9.19", {"center": v(1.36, -1.13) * mm, "radius": 0.09 * mm});
            skCircle(sketch, "E33.2.9.19", {"center": v(1.6, -1.26) * mm, "radius": 0.09 * mm});
            skCircle(sketch, "E33.0.9.20", {"center": v(1.36, -1.36) * mm, "radius": 0.09 * mm});
            skCircle(sketch, "E33.2.9.20", {"center": v(1.6, -1.5) * mm, "radius": 0.09 * mm});
            skCircle(sketch, "E33.0.9.21", {"center": v(1.36, -1.59) * mm, "radius": 0.09 * mm});
            skCircle(sketch, "E33.2.9.21", {"center": v(1.6, -1.72) * mm, "radius": 0.09 * mm});
            skCircle(sketch, "E33.0.10.11", {"center": v(1.82, 0.68) * mm, "radius": 0.09 * mm});
            skCircle(sketch, "E33.2.10.11", {"center": v(2.04, 0.55) * mm, "radius": 0.09 * mm});
            skCircle(sketch, "E33.0.10.12", {"center": v(1.82, 0.46) * mm, "radius": 0.09 * mm});
            skCircle(sketch, "E33.2.10.12", {"center": v(2.04, 0.33) * mm, "radius": 0.09 * mm});
            skCircle(sketch, "E33.0.10.13", {"center": v(1.82, 0.23) * mm, "radius": 0.09 * mm});
            skCircle(sketch, "E33.2.10.13", {"center": v(2.04, 0.1) * mm, "radius": 0.09 * mm});
            skCircle(sketch, "E33.0.10.14", {"center": v(1.82, 0) * mm, "radius": 0.09 * mm});
            skCircle(sketch, "E33.2.10.14", {"center": v(2.04, -0.13) * mm, "radius": 0.09 * mm});
            skCircle(sketch, "E33.0.10.15", {"center": v(1.82, -0.22) * mm, "radius": 0.09 * mm});
            skCircle(sketch, "E33.2.10.15", {"center": v(2.04, -0.36) * mm, "radius": 0.09 * mm});
            skCircle(sketch, "E33.0.10.16", {"center": v(1.82, -0.45) * mm, "radius": 0.09 * mm});
            skCircle(sketch, "E33.2.10.16", {"center": v(2.04, -0.58) * mm, "radius": 0.09 * mm});
            skCircle(sketch, "E33.0.10.17", {"center": v(1.82, -0.68) * mm, "radius": 0.09 * mm});
            skCircle(sketch, "E33.2.10.17", {"center": v(2.04, -0.8) * mm, "radius": 0.09 * mm});
            skCircle(sketch, "E33.0.10.18", {"center": v(1.82, -0.9) * mm, "radius": 0.09 * mm});
            skCircle(sketch, "E33.2.10.18", {"center": v(2.04, -1.04) * mm, "radius": 0.09 * mm});
            skCircle(sketch, "E33.0.10.19", {"center": v(1.82, -1.13) * mm, "radius": 0.09 * mm});
            skCircle(sketch, "E33.2.10.19", {"center": v(2.04, -1.26) * mm, "radius": 0.09 * mm});
            skCircle(sketch, "E33.0.10.20", {"center": v(1.82, -1.36) * mm, "radius": 0.09 * mm});
            skCircle(sketch, "E33.0.10.21", {"center": v(1.82, -1.59) * mm, "radius": 0.09 * mm});
            skCircle(sketch, "E34.0.11.10", {"center": v(2.27, 0.91) * mm, "radius": 0.09 * mm});
            skCircle(sketch, "E34.0.11.11", {"center": v(2.27, 0.68) * mm, "radius": 0.09 * mm});
            skCircle(sketch, "E34.0.11.12", {"center": v(2.27, 0.46) * mm, "radius": 0.09 * mm});
            skCircle(sketch, "E34.0.11.13", {"center": v(2.27, 0.23) * mm, "radius": 0.09 * mm});
            skCircle(sketch, "E34.0.11.14", {"center": v(2.27, 0) * mm, "radius": 0.09 * mm});
            skCircle(sketch, "E34.0.11.15", {"center": v(2.27, -0.22) * mm, "radius": 0.09 * mm});
            skCircle(sketch, "E34.0.11.16", {"center": v(2.27, -0.45) * mm, "radius": 0.09 * mm});
            skCircle(sketch, "E34.0.11.17", {"center": v(2.27, -0.68) * mm, "radius": 0.09 * mm});
            skCircle(sketch, "E34.0.11.18", {"center": v(2.27, -0.9) * mm, "radius": 0.09 * mm});
            skCircle(sketch, "E35.0.3.22", {"center": v(-1.36, -1.81) * mm, "radius": 0.09 * mm});
            skCircle(sketch, "E35.2.3.22", {"center": v(-1.13, -1.94) * mm, "radius": 0.09 * mm});
            skCircle(sketch, "E35.0.3.23", {"center": v(-1.36, -2.04) * mm, "radius": 0.09 * mm});
            skCircle(sketch, "E35.2.3.23", {"center": v(-1.13, -2.17) * mm, "radius": 0.09 * mm});
            skCircle(sketch, "E35.0.4.22", {"center": v(-0.9, -1.81) * mm, "radius": 0.09 * mm});
            skCircle(sketch, "E35.2.4.22", {"center": v(-0.68, -1.94) * mm, "radius": 0.09 * mm});
            skCircle(sketch, "E35.0.4.23", {"center": v(-0.9, -2.04) * mm, "radius": 0.09 * mm});
            skCircle(sketch, "E35.2.4.23", {"center": v(-0.68, -2.17) * mm, "radius": 0.09 * mm});
            skCircle(sketch, "E35.0.4.24", {"center": v(-0.9, -2.27) * mm, "radius": 0.09 * mm});
            skCircle(sketch, "E35.0.5.22", {"center": v(-0.45, -1.81) * mm, "radius": 0.09 * mm});
            skCircle(sketch, "E35.2.5.22", {"center": v(-0.23, -1.94) * mm, "radius": 0.09 * mm});
            skCircle(sketch, "E35.0.5.23", {"center": v(-0.45, -2.04) * mm, "radius": 0.09 * mm});
            skCircle(sketch, "E35.2.5.23", {"center": v(-0.23, -2.17) * mm, "radius": 0.09 * mm});
            skCircle(sketch, "E35.0.5.24", {"center": v(-0.45, -2.27) * mm, "radius": 0.09 * mm});
            skCircle(sketch, "E35.2.5.24", {"center": v(-0.23, -2.4) * mm, "radius": 0.09 * mm});
            skCircle(sketch, "E35.0.6.22", {"center": v(0, -1.81) * mm, "radius": 0.09 * mm});
            skCircle(sketch, "E35.2.6.22", {"center": v(0.23, -1.94) * mm, "radius": 0.09 * mm});
            skCircle(sketch, "E35.0.6.23", {"center": v(0, -2.04) * mm, "radius": 0.09 * mm});
            skCircle(sketch, "E35.2.6.23", {"center": v(0.23, -2.17) * mm, "radius": 0.09 * mm});
            skCircle(sketch, "E35.0.6.24", {"center": v(0, -2.27) * mm, "radius": 0.09 * mm});
            skCircle(sketch, "E35.2.6.24", {"center": v(0.23, -2.4) * mm, "radius": 0.09 * mm});
            skCircle(sketch, "E35.0.7.22", {"center": v(0.45, -1.81) * mm, "radius": 0.09 * mm});
            skCircle(sketch, "E35.2.7.22", {"center": v(0.68, -1.94) * mm, "radius": 0.09 * mm});
            skCircle(sketch, "E35.0.7.23", {"center": v(0.45, -2.04) * mm, "radius": 0.09 * mm});
            skCircle(sketch, "E35.2.7.23", {"center": v(0.68, -2.17) * mm, "radius": 0.09 * mm});
            skCircle(sketch, "E35.0.7.24", {"center": v(0.45, -2.27) * mm, "radius": 0.09 * mm});
            skCircle(sketch, "E35.0.8.22", {"center": v(0.9, -1.81) * mm, "radius": 0.09 * mm});
            skCircle(sketch, "E35.2.8.22", {"center": v(1.14, -1.94) * mm, "radius": 0.09 * mm});
            skCircle(sketch, "E35.0.8.23", {"center": v(0.9, -2.04) * mm, "radius": 0.09 * mm});
            skCircle(sketch, "E35.2.8.23", {"center": v(1.14, -2.17) * mm, "radius": 0.09 * mm});
            skCircle(sketch, "E35.0.8.24", {"center": v(0.9, -2.27) * mm, "radius": 0.09 * mm});
            skCircle(sketch, "E35.0.9.22", {"center": v(1.36, -1.81) * mm, "radius": 0.09 * mm});
            skCircle(sketch, "E35.0.9.23", {"center": v(1.36, -2.04) * mm, "radius": 0.09 * mm});
            skCircle(sketch, "E36.0", {"center": v(0, 0) * mm, "radius": 2.5 * mm, "construction": true});
            skSolve(sketch);
        }
        {
            var Q0;
            Q0=qSketchRegion(id+"F3",true);
            extrude(context, id + "F4", {"entities" : qUnion([Q0]), "operationType" : NewBodyOperationType.REMOVE, "endBound" : BoundingType.THROUGH_ALL, "oppositeDirection" : true, "depth" : 25 * mm});
        }
    });
